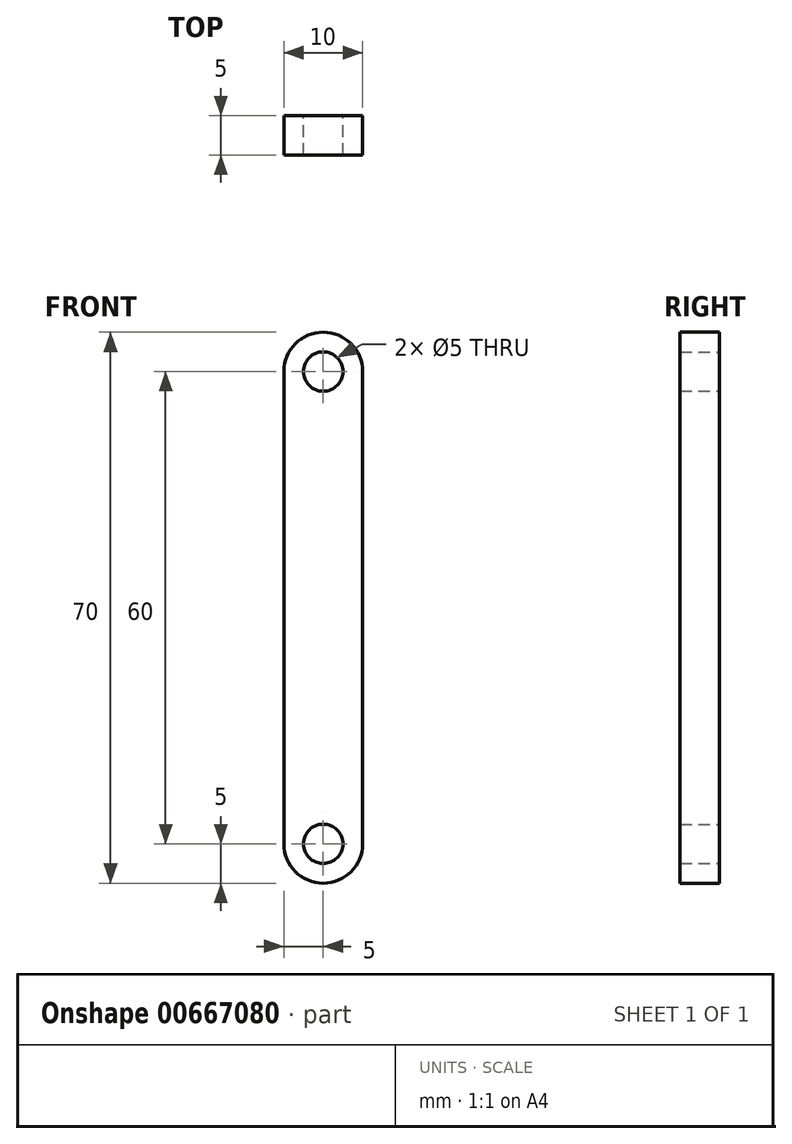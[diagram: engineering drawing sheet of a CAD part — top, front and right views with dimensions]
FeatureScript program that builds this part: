
annotation { "Feature Type Name" : "Feature", "Feature Type Description" : "" }
export const myFeature = defineFeature(function(context is Context, id is Id, definition is map)
    precondition{}
    {
        {
            var Q0;
            Q0=qCreatedBy(makeId("Front.planeOp"),FACE);
            var sketch = newSketch(context, id + "F0", { "sketchPlane" : qUnion([Q0])});
            skArc(sketch, "E0", {"start": v(-5, 0) * mm, "mid": v(0, -5) * mm, "end": v(5, 0) * mm});
            skCircle(sketch, "E1", {"center": v(0, 0) * mm, "radius": 2.5 * mm});
            skArc(sketch, "E2", {"start": v(5, 60) * mm, "mid": v(0, 65) * mm, "end": v(-5, 60) * mm});
            skCircle(sketch, "E3", {"center": v(0, 60) * mm, "radius": 2.5 * mm});
            skLineSegment(sketch, "E4", {"start": v(-5, 60) * mm, "end": v(-5, 0) * mm});
            skLineSegment(sketch, "E5", {"start": v(5, 60) * mm, "end": v(5, 0) * mm});
            skSolve(sketch);
        }
        {
            var Q0;
            Q0=makeQuery(id+"F0.imprint","IMPRINT",FACE,{"disambiguationData":[TD([[makeQuery(id+"F0.imprint","IMPRINT",EDGE,{"derivedFrom":sQuery(id+"F0.wireOp",EDGE,"E0")}),1.0]])]});
            extrude(context, id + "F1", {"entities" : qUnion([Q0]), "endBound" : BoundingType.SYMMETRIC, "depth" : 5 * mm, "offsetDistance" : 25 * mm});
        }
    });
